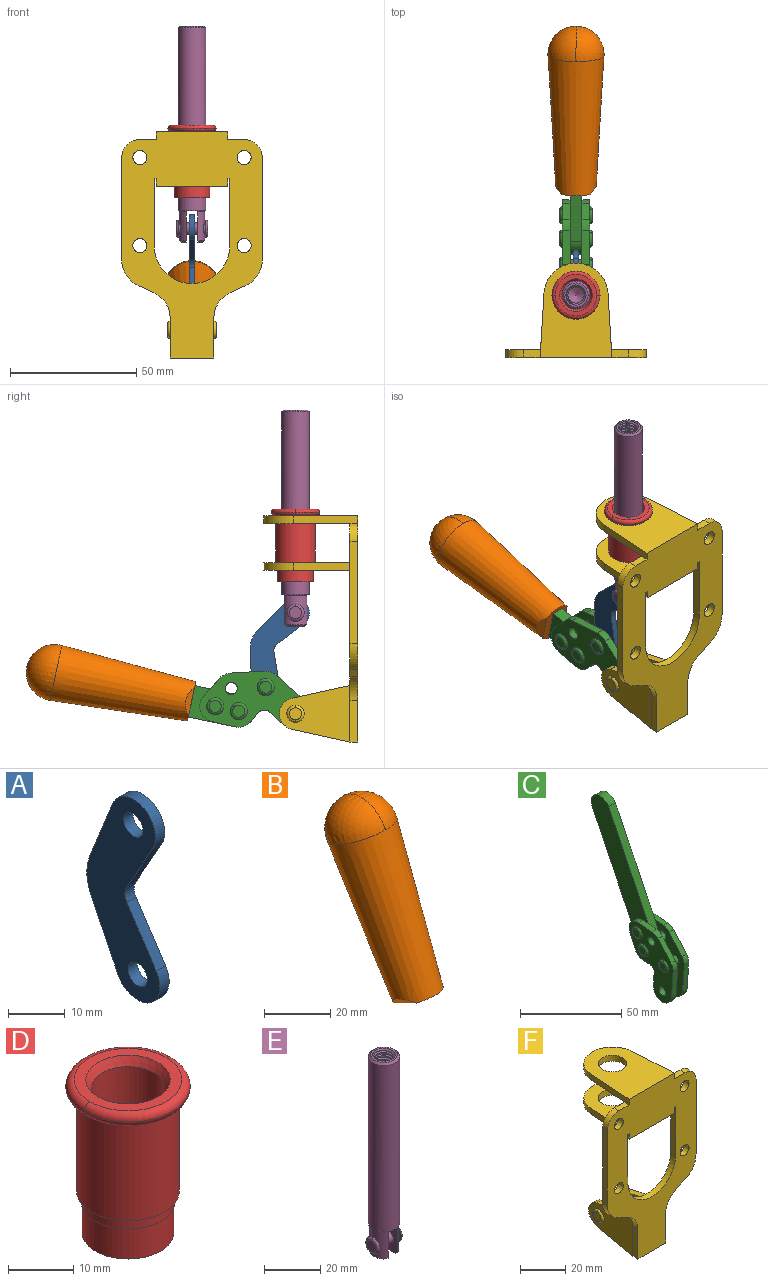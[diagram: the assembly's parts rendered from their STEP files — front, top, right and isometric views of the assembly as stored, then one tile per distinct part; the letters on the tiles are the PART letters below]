
ASSEMBLY  parts=6 mates=6
PART A: 12 faces, bbox 2.3x18.2x42.8 mm
  f0: cylinder r=2.4mm len=4.8mm, axis (1,0,0), area 34.9mm2, adj f4,f11
  f1: cylinder r=10.41mm len=8.47mm, axis (1,0,0), area 20.2mm2, adj f4,f9,f10,f11
  f2: cylinder r=3.05mm len=3.16mm, axis (1,0,0), area 7.7mm2, adj f4,f6,f7,f11
  f3: cylinder r=2.4mm len=4.8mm, axis (1,0,0), area 34.9mm2, adj f4,f11
  f4: plane 42.81x18.23mm, normal (-1,0,0), area 414.1mm2, adj f0,f1,f2,f3,f5,f6,f7,f8
  f5: cylinder r=5.54mm len=10.67mm, axis (1,0,0), area 41.8mm2, adj f4,f6,f10,f11
  f6: plane 11.66x6.53mm, normal (0,-0.87,-0.49), area 30.9mm2, adj f2,f4,f5,f11
  f7: plane 11.17x7.33mm, normal (0,-0.84,0.55), area 30.9mm2, adj f2,f4,f8,f11
  f8: cylinder r=5.54mm len=10.51mm, axis (1,0,0), area 41.8mm2, adj f4,f7,f9,f11
  f9: plane 13.67x6.67mm, normal (0,0.9,-0.44), area 35.1mm2, adj f1,f4,f8,f11
  f10: plane 14.1x5.7mm, normal (0,0.93,0.37), area 35.1mm2, adj f1,f4,f5,f11
  f11: plane 42.81x18.23mm, normal (1,0,0), area 414.1mm2, adj f0,f1,f2,f3,f5,f6,f7,f8
PART B: 11 faces, bbox 22.3x42.6x64.5 mm
  f0: sphere r=11.13mm, area 411.4mm2, adj f1,f8
  f1: cone r=11.11mm half-angle=3.3deg, axis (0,0.44,0.9), area 3251.8mm2, adj f0,f7,f8,f9,f10
  f2: cylinder r=6.16mm len=11.7mm, axis (1,0,0), area 89.5mm2, adj f3,f4,f5,f6
  f3: plane 60.23x36.75mm, normal (-1,0,0), area 763.6mm2, adj f2,f4,f6,f10
  f4: plane 51.37x25.05mm, normal (0,0.9,-0.44), area 264.2mm2, adj f2,f3,f5,f10
  f5: plane 60.23x36.75mm, normal (1,0,0), area 763.6mm2, adj f2,f4,f6,f10
  f6: plane 51.37x25.05mm, normal (0,-0.9,0.44), area 264.2mm2, adj f2,f3,f5,f10
  f7: plane 9.95x5.95mm, normal (0.71,-0.31,-0.64), area 25.8mm2, adj f1,f10
  f8: sphere r=11.13mm, area 411.4mm2, adj f0,f1
  f9: plane 9.95x5.95mm, normal (-0.71,-0.31,-0.64), area 25.8mm2, adj f1,f10
  f10: plane 14.27x11.38mm, normal (0,-0.44,-0.9), area 106.7mm2, adj f1,f3,f4,f5,f6,f7,f9
PART C: 59 faces, bbox 12.9x60.2x99.6 mm
  f0: torus R=2.39mm, axis (-1,0,0), area 14.9mm2, adj f20,f43,f51
  f1: torus R=2.39mm, axis (-1,0,0), area 14.9mm2, adj f19,f42,f51
  f2: torus R=2.39mm, axis (-1,0,0), area 14.9mm2, adj f18,f35,f51
  f3: torus R=2.39mm, axis (-1,0,0), area 14.9mm2, adj f14,f17,f23
  f4: torus R=2.39mm, axis (-1,0,0), area 14.9mm2, adj f13,f16,f23
  f5: torus R=2.39mm, axis (-1,0,0), area 14.9mm2, adj f12,f15,f23
  f6: cylinder r=2.39mm len=4.78mm, axis (1,0,0), area 46.5mm2, adj f48,f50,f51
  f7: cylinder r=2.39mm len=4.78mm, axis (1,0,0), area 46.5mm2, adj f50,f51
  f8: cylinder r=6.35mm len=12.68mm, axis (1,0,0), area 61.8mm2, adj f38,f39,f50,f51
  f9: cylinder r=2.39mm len=4.78mm, axis (-1,0,0), area 70.5mm2, adj f46,f50
  f10: cylinder r=2.39mm len=4.78mm, axis (-1,0,0), area 46.5mm2, adj f23,f45,f46
  f11: cylinder r=2.39mm len=4.78mm, axis (-1,0,0), area 46.5mm2, adj f23,f46
  f12: plane 4.78x4.78mm, normal (1,0,0), area 17.9mm2, adj f5,f15
  f13: plane 4.78x4.78mm, normal (1,0,0), area 17.9mm2, adj f4,f16
  f14: plane 4.78x4.78mm, normal (1,0,0), area 17.9mm2, adj f3,f17
  f15: torus R=2.39mm, axis (-1,0,0), area 14.9mm2, adj f5,f12,f23
  f16: torus R=2.39mm, axis (-1,0,0), area 14.9mm2, adj f4,f13,f23
  f17: torus R=2.39mm, axis (-1,0,0), area 14.9mm2, adj f3,f14,f23
  f18: plane 4.78x4.78mm, normal (-1,0,0), area 17.9mm2, adj f2,f35
  f19: plane 4.78x4.78mm, normal (-1,0,0), area 17.9mm2, adj f1,f42
  f20: plane 4.78x4.78mm, normal (-1,0,0), area 17.9mm2, adj f0,f43
  f21: plane 2.26x0.2mm, normal (1,0,0), area 0.2mm2, adj f31,f44
  f22: plane 2.26x0.2mm, normal (-1,0,0), area 0.2mm2, adj f41,f44
  f23: plane 39.37x30.77mm, normal (1,0,0), area 565.5mm2, adj f3,f4,f5,f10,f11,f15,f16,f17
  f24: cylinder r=6.1mm len=4.15mm, axis (-1,0,0), area 14.7mm2, adj f23,f25,f32,f46
  f25: plane 10.25x9.01mm, normal (0,-0.75,0.66), area 42.3mm2, adj f23,f24,f26,f46
  f26: cylinder r=6.35mm len=4.64mm, axis (-1,0,0), area 15.6mm2, adj f23,f25,f27,f46
  f27: plane 15.84x3.1mm, normal (0,-1,-0.07), area 49.2mm2, adj f23,f26,f28,f46
  f28: cylinder r=6.35mm len=12.68mm, axis (-1,0,0), area 61.8mm2, adj f23,f27,f29,f46
  f29: plane 8.11x3.1mm, normal (0,1,0.07), area 25.2mm2, adj f23,f28,f30,f46
  f30: cylinder r=3.05mm len=3.25mm, axis (-1,0,0), area 14.8mm2, adj f23,f29,f31,f46
  f31: plane 5.99x3.1mm, normal (0,0.07,-1), area 18.6mm2, adj f21,f23,f30,f44,f46
  f32: plane 9.5x3.1mm, normal (0,-0.07,1), area 29.5mm2, adj f23,f24,f33,f46,f47
  f33: cylinder r=6.1mm len=8.63mm, axis (-1,0,0), area 39.1mm2, adj f23,f32,f34,f47
  f34: plane 8.65x3.96mm, normal (0,0.91,-0.42), area 29.5mm2, adj f23,f33,f44,f47
  f35: torus R=2.39mm, axis (-1,0,0), area 14.9mm2, adj f2,f18,f51
  f36: plane 10.25x9.01mm, normal (0,-0.75,0.66), area 42.3mm2, adj f37,f49,f50,f51
  f37: cylinder r=6.35mm len=4.64mm, axis (1,0,0), area 15.6mm2, adj f36,f38,f50,f51
  f38: plane 15.84x3.1mm, normal (0,-1,-0.07), area 49.2mm2, adj f8,f37,f50,f51
  f39: plane 8.11x3.1mm, normal (0,1,0.07), area 25.2mm2, adj f8,f40,f50,f51
  f40: cylinder r=3.05mm len=3.25mm, axis (1,0,0), area 14.8mm2, adj f39,f41,f50,f51
  f41: plane 5.99x3.1mm, normal (0,0.07,-1), area 18.6mm2, adj f22,f40,f44,f50,f51
  f42: torus R=2.39mm, axis (-1,0,0), area 14.9mm2, adj f1,f19,f51
  f43: torus R=2.39mm, axis (-1,0,0), area 14.9mm2, adj f0,f20,f51
  f44: cylinder r=6.35mm len=12.12mm, axis (-1,0,0), area 128.9mm2, adj f21,f22,f23,f31,f34,f41,f46,f47
  f45: plane 2.65x1.35mm, normal (1,0,0), area 1mm2, adj f10,f55
  f46: plane 39.08x20.42mm, normal (-1,0,0), area 412.5mm2, adj f9,f10,f11,f24,f25,f26,f27,f28
  f47: plane 77.62x39.82mm, normal (1,0,0), area 850mm2, adj f32,f33,f34,f44,f53,f54,f55
  f48: plane 2.65x1.35mm, normal (-1,0,0), area 1mm2, adj f6,f55
  f49: cylinder r=6.1mm len=4.15mm, axis (1,0,0), area 14.7mm2, adj f36,f50,f51,f56
  f50: plane 39.08x20.42mm, normal (1,0,0), area 412.5mm2, adj f6,f7,f8,f9,f36,f37,f38,f39
  f51: plane 39.37x30.77mm, normal (-1,0,0), area 565.5mm2, adj f0,f1,f2,f6,f7,f8,f35,f36
  f52: plane 8.65x3.96mm, normal (0,0.91,-0.42), area 29.5mm2, adj f44,f51,f57,f58
  f53: plane 68.49x33.4mm, normal (0,0.9,-0.44), area 358.1mm2, adj f44,f47,f54,f58
  f54: cylinder r=6.35mm len=12.06mm, axis (1,0,0), area 93.7mm2, adj f47,f53,f55,f58
  f55: plane 68.49x33.4mm, normal (0,-0.9,0.44), area 358.1mm2, adj f44,f45,f46,f47,f48,f50,f54,f58
  f56: plane 9.5x3.1mm, normal (0,-0.07,1), area 29.5mm2, adj f49,f50,f51,f57,f58
  f57: cylinder r=6.1mm len=8.63mm, axis (1,0,0), area 39.1mm2, adj f51,f52,f56,f58
  f58: plane 77.62x39.82mm, normal (-1,0,0), area 850mm2, adj f44,f52,f53,f54,f55,f56,f57
PART D: 15 faces, bbox 20.6x20.6x28.7 mm
  f0: torus R=8.26mm, axis (0,0,1), area 56.8mm2, adj f1,f10,f12
  f1: torus R=8.26mm, axis (0,0,1), area 56.8mm2, adj f0,f6,f13
  f2: cylinder r=5.59mm len=25.91mm, axis (0,0,1), area 909.6mm2, adj f3,f4
  f3: cone r=6.86mm half-angle=45deg, axis (0,0,-1), area 70.2mm2, adj f2,f14
  f4: cone r=6.47mm half-angle=30deg, axis (0,0,1), area 66.7mm2, adj f2,f13
  f5: cylinder r=7.04mm len=14.07mm, axis (0,0,1), area 252.6mm2, adj f11,f14
  f6: torus R=8.26mm, axis (0,0,1), area 56.8mm2, adj f1,f12,f13
  f7: cylinder r=7.16mm len=14.33mm, axis (0,0,1), area 91.5mm2, adj f9,f11
  f8: cylinder r=7.86mm len=18.42mm, axis (0,0,1), area 909.6mm2, adj f9,f10
  f9: plane 15.72x15.72mm, normal (0,0,-1), area 33mm2, adj f7,f8
  f10: plane 16.51x16.51mm, normal (0,0,-1), area 19.9mm2, adj f0,f8,f12
  f11: plane 14.33x14.33mm, normal (0,0,-1), area 5.7mm2, adj f5,f7
  f12: torus R=8.26mm, axis (0,0,1), area 56.8mm2, adj f0,f6,f10
  f13: plane 16.51x16.51mm, normal (0,0,1), area 82.7mm2, adj f1,f4,f6
  f14: plane 14.07x14.07mm, normal (0,0,-1), area 7.8mm2, adj f3,f5
PART E: 48 faces, bbox 12.6x11.1x86.1 mm
  f0: torus R=2.41mm, axis (-1,0,0), area 15mm2, adj f30,f32,f34
  f1: torus R=2.41mm, axis (-1,0,0), area 15mm2, adj f29,f31,f33
  f2: cylinder r=5.54mm len=72.39mm, axis (0,0,1), area 2518.5mm2, adj f3,f4,f42,f43
  f3: cone r=5.54mm half-angle=45deg, axis (0,0,1), area 7.6mm2, adj f2,f5,f41
  f4: cone r=5.54mm half-angle=45deg, axis (0,0,-1), area 34.9mm2, adj f2,f39
  f5: cylinder r=5.08mm len=11.48mm, axis (0,0,1), area 108.3mm2, adj f3,f7,f8,f41
  f6: cylinder r=2.41mm len=4.83mm, axis (-1,0,0), area 71.2mm2, adj f40,f41
  f7: cylinder r=2.41mm len=4.83mm, axis (-1,0,0), area 7.6mm2, adj f5,f34
  f8: cone r=5.08mm half-angle=45deg, axis (0,0,1), area 10.6mm2, adj f5,f37,f41
  f9: cone r=3.98mm half-angle=45deg, axis (0,0,1), area 17.6mm2, adj f27,f39,f45,f46,f47
  f10: cylinder r=2.41mm len=4.83mm, axis (-1,0,0), area 7.6mm2, adj f33,f38
  f11: cylinder r=3.2mm len=6.4mm, axis (0,0,1), area 78.4mm2, adj f12,f28,f44,f45,f47
  f12: cylinder r=3.2mm len=6.4mm, axis (0,0,1), area 10.5mm2, adj f11,f13,f45,f47
  f13: cylinder r=3.2mm len=6.4mm, axis (0,0,1), area 10.5mm2, adj f12,f14,f45,f47
  f14: cylinder r=3.2mm len=6.4mm, axis (0,0,1), area 10.5mm2, adj f13,f15,f45,f47
  f15: cylinder r=3.2mm len=6.4mm, axis (0,0,1), area 10.5mm2, adj f14,f16,f45,f47
  f16: cylinder r=3.2mm len=6.4mm, axis (0,0,1), area 10.5mm2, adj f15,f17,f45,f47
  f17: cylinder r=3.2mm len=6.4mm, axis (0,0,1), area 10.5mm2, adj f16,f18,f45,f47
  f18: cylinder r=3.2mm len=6.4mm, axis (0,0,1), area 10.5mm2, adj f17,f19,f45,f47
  f19: cylinder r=3.2mm len=6.4mm, axis (0,0,1), area 10.5mm2, adj f18,f20,f45,f47
  f20: cylinder r=3.2mm len=6.4mm, axis (0,0,1), area 10.5mm2, adj f19,f21,f45,f47
  f21: cylinder r=3.2mm len=6.4mm, axis (0,0,1), area 10.5mm2, adj f20,f22,f45,f47
  f22: cylinder r=3.2mm len=6.4mm, axis (0,0,1), area 10.5mm2, adj f21,f23,f45,f47
  f23: cylinder r=3.2mm len=6.4mm, axis (0,0,1), area 10.5mm2, adj f22,f24,f45,f47
  f24: cylinder r=3.2mm len=6.4mm, axis (0,0,1), area 10.5mm2, adj f23,f25,f45,f47
  f25: cylinder r=3.2mm len=6.4mm, axis (0,0,1), area 10.5mm2, adj f24,f26,f45,f47
  f26: cylinder r=3.2mm len=6.4mm, axis (0,0,1), area 10.5mm2, adj f25,f27,f45,f47
  f27: cylinder r=3.2mm len=6.4mm, axis (0,0,1), area 7.4mm2, adj f9,f26,f45,f47
  f28: cone r=3.2mm half-angle=60deg, axis (0,0,1), area 37.2mm2, adj f11
  f29: plane 4.83x4.83mm, normal (-1,0,0), area 18.3mm2, adj f1,f31
  f30: plane 4.83x4.83mm, normal (1,0,0), area 18.3mm2, adj f0,f32
  f31: torus R=2.41mm, axis (-1,0,0), area 15mm2, adj f1,f29,f33
  f32: torus R=2.41mm, axis (-1,0,0), area 15mm2, adj f0,f30,f34
  f33: plane 6.83x6.83mm, normal (1,0,0), area 18.3mm2, adj f1,f10,f31
  f34: plane 6.83x6.83mm, normal (-1,0,0), area 18.3mm2, adj f0,f7,f32
  f35: cone r=5.08mm half-angle=45deg, axis (0,0,1), area 10.6mm2, adj f36,f38,f40
  f36: plane 7.25x1.97mm, normal (0,0,-1), area 10mm2, adj f35,f40
  f37: plane 7.25x1.97mm, normal (0,0,-1), area 10mm2, adj f8,f41
  f38: cylinder r=5.08mm len=11.48mm, axis (0,0,1), area 108.3mm2, adj f10,f35,f40,f42
  f39: plane 9.55x9.55mm, normal (0,0,1), area 22mm2, adj f4,f9
  f40: plane 12.76x10.09mm, normal (1,0,0), area 95.7mm2, adj f6,f35,f36,f38,f42,f43
  f41: plane 12.76x10.09mm, normal (-1,0,0), area 95.7mm2, adj f3,f5,f6,f8,f37,f43
  f42: cone r=5.54mm half-angle=45deg, axis (0,0,1), area 7.6mm2, adj f2,f38,f40
  f43: plane 11.07x4.7mm, normal (0,0,-1), area 50.4mm2, adj f2,f40,f41
  f44: plane 0.89x0.62mm, normal (-1,0,0), area 0.3mm2, adj f11,f45,f46,f47
  f45: bspline ~24.8x7.63mm, area 266.6mm2, adj f9,f11,f12,f13,f14,f15,f16,f17
  f46: bspline ~24.87x7.63mm, area 73.6mm2, adj f9,f44,f45,f47
  f47: bspline ~24.98x7.63mm, area 272.5mm2, adj f9,f11,f12,f13,f14,f15,f16,f17
PART F: 55 faces, bbox 55.7x37.4x89.8 mm
  f0: torus R=2.41mm, axis (-1,0,0), area 15mm2, adj f11,f15,f25
  f1: torus R=2.41mm, axis (-1,0,0), area 15mm2, adj f10,f12,f22
  f2: cylinder r=2.78mm len=5.56mm, axis (0,-1,0), area 54.2mm2, adj f30,f54
  f3: cylinder r=14.99mm len=29.97mm, axis (0,-1,0), area 145.9mm2, adj f30,f49,f53,f54
  f4: cylinder r=2.78mm len=5.56mm, axis (0,-1,0), area 54.2mm2, adj f30,f54
  f5: cylinder r=2.78mm len=5.56mm, axis (0,-1,0), area 54.2mm2, adj f30,f54
  f6: cylinder r=2.78mm len=5.56mm, axis (0,-1,0), area 54.2mm2, adj f30,f54
  f7: cylinder r=6.35mm len=12.7mm, axis (0,0,1), area 123.6mm2, adj f27,f51
  f8: cylinder r=6.35mm len=12.7mm, axis (0,0,-1), area 124.7mm2, adj f21,f35
  f9: cylinder r=2.41mm len=11.18mm, axis (-1,0,0), area 169.4mm2, adj f16,f19
  f10: plane 4.83x4.83mm, normal (1,0,0), area 18.3mm2, adj f1,f12
  f11: plane 4.83x4.83mm, normal (-1,0,0), area 18.3mm2, adj f0,f15
  f12: torus R=2.41mm, axis (-1,0,0), area 15mm2, adj f1,f10,f22
  f13: cylinder r=6.35mm len=12.41mm, axis (1,0,0), area 53.4mm2, adj f18,f19,f22,f23
  f14: cylinder r=6.35mm len=12.41mm, axis (-1,0,0), area 53.4mm2, adj f16,f17,f24,f25
  f15: torus R=2.41mm, axis (-1,0,0), area 15mm2, adj f0,f11,f25
  f16: plane 27.86x22.35mm, normal (1,0,0), area 425.4mm2, adj f9,f14,f17,f24,f30
  f17: plane 22.86x4.97mm, normal (0,0.21,0.98), area 72.5mm2, adj f14,f16,f25,f30
  f18: plane 22.86x4.97mm, normal (0,0.21,0.98), area 72.5mm2, adj f13,f19,f22,f30
  f19: plane 27.86x22.35mm, normal (-1,0,0), area 425.4mm2, adj f9,f13,f18,f23,f30
  f20: cylinder r=12.7mm len=25.35mm, axis (0,0,-1), area 119.8mm2, adj f21,f34,f35,f36
  f21: plane 34.21x28.07mm, normal (0,0,-1), area 702.4mm2, adj f8,f20,f30,f34,f36
  f22: plane 27.96x22.45mm, normal (1,0,0), area 407.2mm2, adj f1,f12,f13,f18,f23,f30,f42,f43
  f23: plane 22.86x4.97mm, normal (0,0.21,-0.98), area 72.5mm2, adj f13,f19,f22,f44
  f24: plane 22.86x4.97mm, normal (0,0.21,-0.98), area 72.5mm2, adj f14,f16,f25,f44
  f25: plane 27.86x22.35mm, normal (-1,0,0), area 407.1mm2, adj f0,f14,f15,f17,f24,f30,f45,f46
  f26: plane 3.1x0.95mm, normal (0,0,-1), area 2.7mm2, adj f30,f49,f50,f54
  f27: plane 34.21x28.07mm, normal (0,0,1), area 702.4mm2, adj f7,f28,f30,f50,f52
  f28: cylinder r=12.7mm len=25.35mm, axis (0,0,1), area 118.8mm2, adj f27,f50,f51,f52
  f29: plane 3.1x0.95mm, normal (0,0,-1), area 2.7mm2, adj f30,f52,f53,f54
  f30: plane 86.54x55.63mm, normal (0,1,0), area 2362.9mm2, adj f2,f3,f4,f5,f6,f16,f17,f18
  f31: plane 40.56x3.1mm, normal (-1,0,0), area 125.7mm2, adj f30,f32,f48,f54
  f32: cylinder r=7.11mm len=7.11mm, axis (0,-1,0), area 34.6mm2, adj f30,f31,f33,f54
  f33: plane 6.67x3.1mm, normal (0,0,1), area 20.4mm2, adj f30,f32,f34,f54
  f34: plane 25.39x3.13mm, normal (-1,0.06,0), area 79.5mm2, adj f20,f21,f33,f35,f54
  f35: plane 37.31x28.45mm, normal (0,0,1), area 789.9mm2, adj f8,f20,f34,f36,f54
  f36: plane 25.39x3.13mm, normal (1,0.06,0), area 79.5mm2, adj f20,f21,f35,f37,f54
  f37: plane 6.67x3.1mm, normal (0,0,1), area 20.4mm2, adj f30,f36,f38,f54
  f38: cylinder r=7.11mm len=7.11mm, axis (0,-1,0), area 34.6mm2, adj f30,f37,f39,f54
  f39: plane 40.56x3.1mm, normal (1,0,0), area 125.7mm2, adj f30,f38,f40,f54
  f40: cylinder r=11.18mm len=10.16mm, axis (0,-1,0), area 39.5mm2, adj f30,f39,f41,f54
  f41: plane 6.09x3.1mm, normal (0.42,0,-0.91), area 20.8mm2, adj f30,f40,f42,f54
  f42: cylinder r=11.18mm len=9.41mm, axis (0,-1,0), area 37.2mm2, adj f22,f30,f41,f43,f54
  f43: plane 16.5x3.1mm, normal (1,0,0), area 51.1mm2, adj f22,f42,f44,f54
  f44: plane 17.37x3.1mm, normal (0,0,-1), area 53.8mm2, adj f23,f24,f30,f43,f45,f54
  f45: plane 16.5x3.1mm, normal (-1,0,0), area 51.1mm2, adj f25,f44,f46,f54
  f46: cylinder r=11.18mm len=9.41mm, axis (0,-1,0), area 37.2mm2, adj f25,f30,f45,f47,f54
  f47: plane 6.09x3.1mm, normal (-0.42,0,-0.91), area 20.8mm2, adj f30,f46,f48,f54
  f48: cylinder r=11.18mm len=10.16mm, axis (0,-1,0), area 39.5mm2, adj f30,f31,f47,f54
  f49: plane 26.54x3.1mm, normal (-1,0,0), area 82.3mm2, adj f3,f26,f30,f54
  f50: plane 25.39x3.1mm, normal (1,0.06,0), area 78.8mm2, adj f26,f27,f28,f51,f54
  f51: plane 37.31x28.45mm, normal (0,0,-1), area 789.9mm2, adj f7,f28,f50,f52,f54
  f52: plane 25.39x3.1mm, normal (-1,0.06,0), area 78.8mm2, adj f27,f28,f29,f51,f54
  f53: plane 26.54x3.1mm, normal (1,0,0), area 82.3mm2, adj f3,f29,f30,f54
  f54: plane 89.66x55.63mm, normal (0,-1,0), area 2678.5mm2, adj f2,f3,f4,f5,f6,f26,f29,f31
PLACE A rot(axis=(1,0,0),23.9deg) t=(-5.39,6.81,-23.07)mm
PLACE B rot(axis=(-1,0,0),52.1deg) t=(-5.39,33.29,0.11)mm
PLACE C rot(axis=(-1,0,0),52.1deg) t=(-5.39,33.29,0.11)mm
PLACE D t=(-5.39,-1.55,-6.92)mm
PLACE E t=(-5.39,-1.55,-14.43)mm
PLACE F t=(-5.39,-1.55,-6.92)mm fixed
MATE fastened D.f0 <-> F.f7  axis (0,0,-1) through (-5.39,23.06,39.47)mm
MATE slider E.f2 <-> D.f2  axis (0,0,1) through (-5.39,23.06,44.35)mm
MATE revolute C.f7 <-> F.f0  axis (-1,0,0) through (-5.39,23.06,-39.02)mm
MATE revolute A.f3 <-> C.f4  axis (1,0,0) through (-5.39,34.88,-28.42)mm
MATE revolute A.f5 <-> E.f6  axis (1,0,0) through (-5.39,23.06,1.04)mm
MATE fastened B.f2 <-> C.f54  axis (1,0,0) through (-5.39,120.14,-22.36)mm
